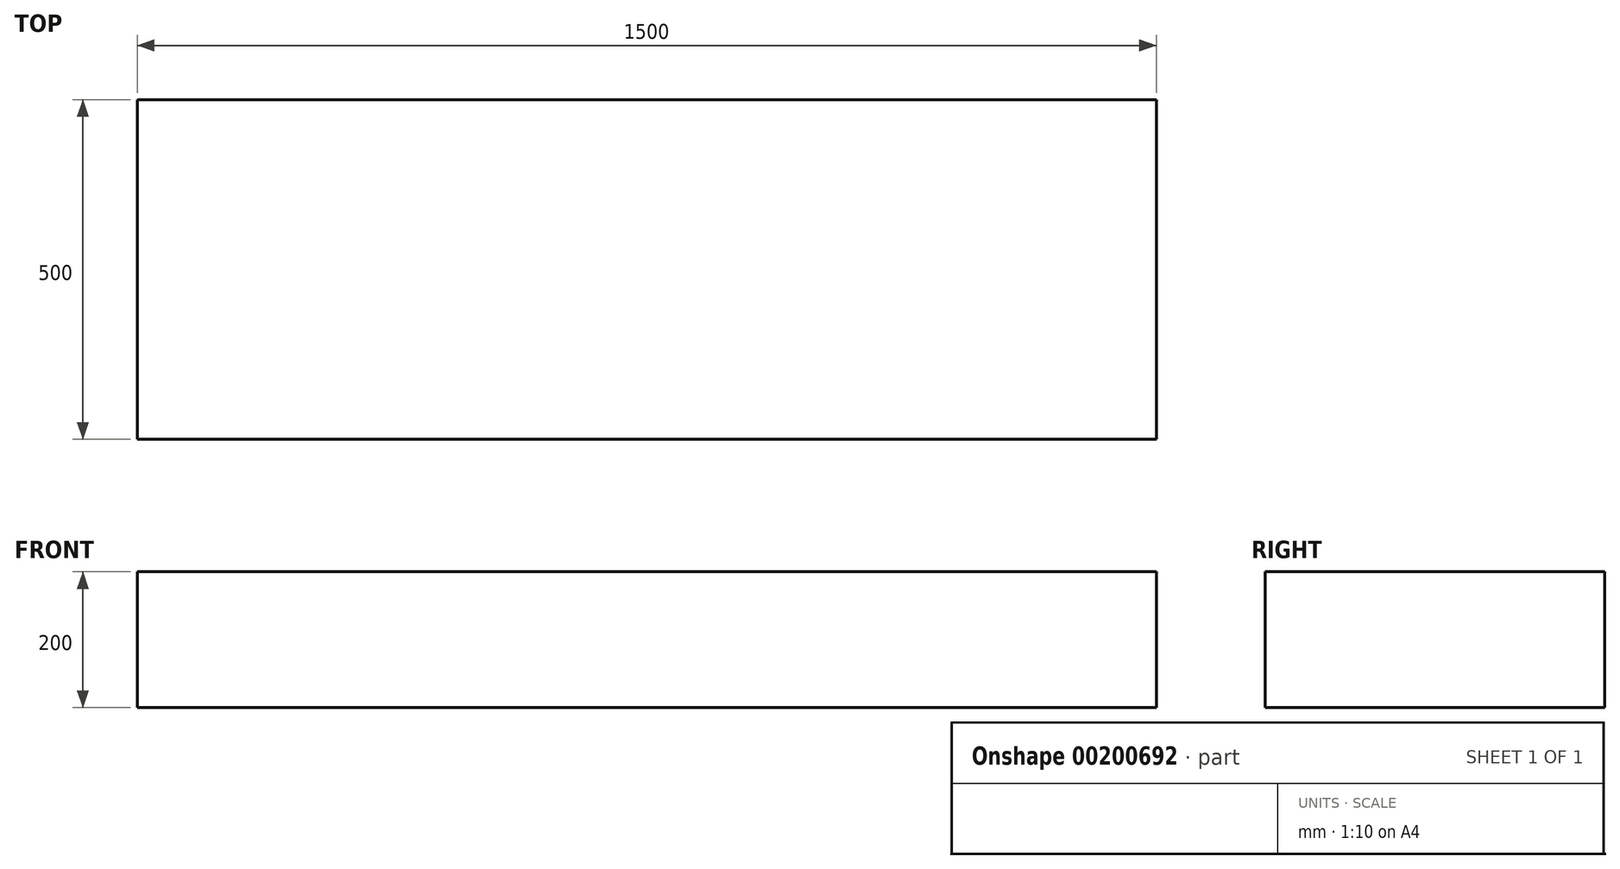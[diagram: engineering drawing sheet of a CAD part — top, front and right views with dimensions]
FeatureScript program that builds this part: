
annotation { "Feature Type Name" : "Feature", "Feature Type Description" : "" }
export const myFeature = defineFeature(function(context is Context, id is Id, definition is map)
    precondition{}
    {
        {
            var Q0;
            Q0=qCreatedBy(makeId("Front.planeOp"),FACE);
            var sketch = newSketch(context, id + "F0", { "sketchPlane" : qUnion([Q0])});
            skLineSegment(sketch, "E0.bottom", {"start": v(0, 0) * mm, "end": v(1500, 0) * mm});
            skLineSegment(sketch, "E0.top", {"start": v(0, 200) * mm, "end": v(1500, 200) * mm});
            skLineSegment(sketch, "E0.left", {"start": v(0, 0) * mm, "end": v(0, 200) * mm});
            skLineSegment(sketch, "E0.right", {"start": v(1500, 0) * mm, "end": v(1500, 200) * mm});
            skSolve(sketch);
        }
        {
            var Q0;
            Q0=qSketchRegion(id+"F0",true);
            extrude(context, id + "F1", {"entities" : qUnion([Q0]), "depth" : 500 * mm});
        }
    });
